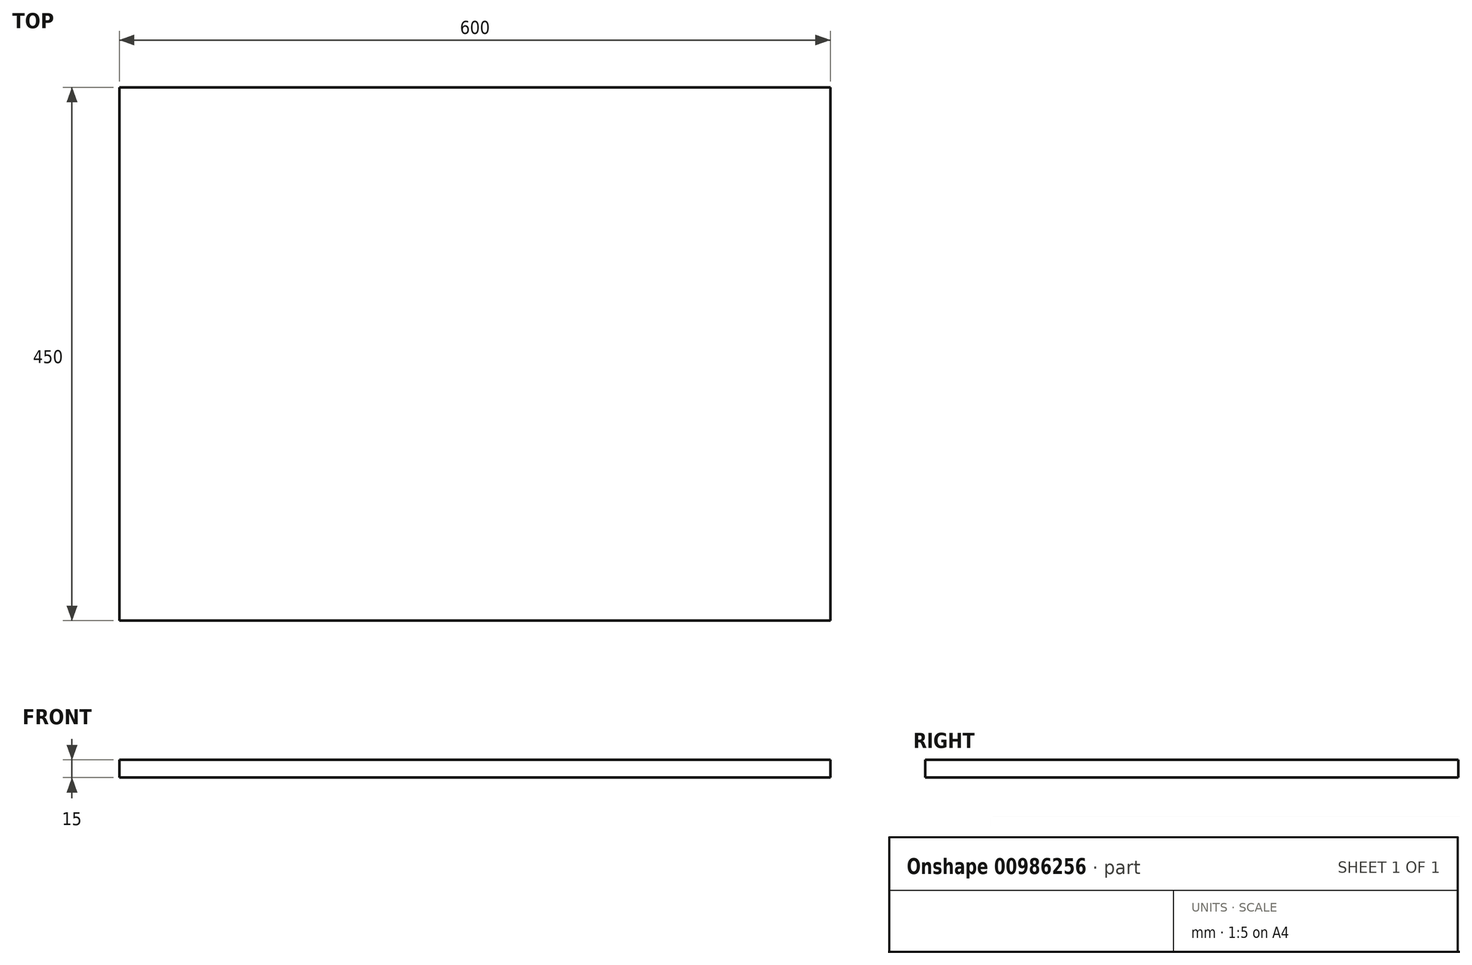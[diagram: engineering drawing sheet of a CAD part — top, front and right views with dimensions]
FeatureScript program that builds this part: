
annotation { "Feature Type Name" : "Feature", "Feature Type Description" : "" }
export const myFeature = defineFeature(function(context is Context, id is Id, definition is map)
    precondition{}
    {
        {
            var Q0;
            Q0=qCreatedBy(makeId("Top.planeOp"),FACE);
            var sketch = newSketch(context, id + "F0", { "sketchPlane" : qUnion([Q0])});
            skLineSegment(sketch, "E0.bottom", {"start": v(-304.76, 274.94) * mm, "end": v(295.24, 274.94) * mm});
            skLineSegment(sketch, "E0.top", {"start": v(-304.76, -175.06) * mm, "end": v(295.24, -175.06) * mm});
            skLineSegment(sketch, "E0.left", {"start": v(-304.76, 274.94) * mm, "end": v(-304.76, -175.06) * mm});
            skLineSegment(sketch, "E0.right", {"start": v(295.24, 274.94) * mm, "end": v(295.24, -175.06) * mm});
            skSolve(sketch);
        }
        {
            var Q0;
            Q0 = qSketchRegion(id + "F0", true);
            extrude(context, id + "F1", {"entities" : qUnion([Q0]), "depth" : 15 * mm, "offsetDistance" : 25 * mm});
        }
    });
